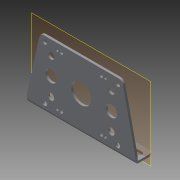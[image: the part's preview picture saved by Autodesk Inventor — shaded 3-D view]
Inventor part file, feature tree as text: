
AUTODESK INVENTOR PART (.ipt)
format: ipt  version: 2015 SP1 (Build 190203100, 203)  size: 150,528 bytes
history: native  units: in
note: dims shown in document units (in); Inventor stores cm internally (conversion verified against a paired STEP export)
features: other x2, plane x1, imported_body x1
ambient origin geometry x8: Origin, YZ Plane, XZ Plane, XY Plane, X Axis, Y Axis, Z Axis, Center Point
bodies: Body1 (feature_tree)
feature tree (4):
  other  "Single_d02"
  other  "Single_d02.ipt1"
  plane  "Work Plane1"
  imported_body  "Base1"
